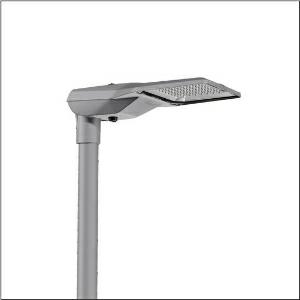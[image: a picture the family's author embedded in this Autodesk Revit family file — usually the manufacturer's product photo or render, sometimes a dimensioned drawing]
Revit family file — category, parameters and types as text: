
# Revit family: streetlight_sl_21_iq_midi___pc-l_5xe3f31y08mb_244c
name_source: partatom
category: Lighting Fixtures
units: mm (PartAtom-declared; Revit-internal decimal feet)

## family parameters
Cut with Voids When Loaded = No
Host = Face
Light Source = No
Part Type = Normal
Room Calculation Point = No
Round Connector Dimension = Use Diameter
Shared = No

## types (1)
- --- (1 x LED, 17070 lm, 129.3 W, 3000K)
    Apparent Load = 129 VA
    CIE Flux Codes = 38 78 98 100 100
    Color Rendering = 70
    Color Temperature = 3000K
    Default Elevation = 1800 mm
    Description = Streetlight SL 21 iQ midi, mast luminaire, primary light control with lens, of PMMA, primary optical cover: cover, of toughened safety glass, transparent, light distribution: PC-L, light emission: direct distribution, primary light characteristic: asymmetric, left, installation type: post-top, side-entry, LED, High Power LED, rated luminous flux: 17.070lm, luminous efficacy: 132lm/W, light colour: 730, colour temperature: 3000K, control gear: iQ-Street Remote, D4i with power reduction, control: pre-setting: logarithmic dimming characteristic, Street-Remote, Auto-Match, Temp-Guard, Lumen-Switch, Night-Set, Smart-Wire, Light-Fading, Desk-Remote (wireless, voltage-free reading and setting of iQ features in the workshop via application-optimized NFC function/RFID function), optimised constant luminous flux control (CLO 2.0), mains connection: 230..240V, AC, 50/60Hz, start of lifetime: 129W, end of service life: 142W, reduction: 56W, luminaire housing, of diecast aluminium, powder-coated, Siteco® metallic grey (DB 702S), corrosivity category C5 mid according to DIN EN ISO 12944, please order mast flange separately, inclination adjustable: 0°, 5°, 10°, 15°, sealing non-destructively replaceable, multi-level sealing system, length: 644mm, width: 335mm, height: 110mm, mast flange for spigot size: 42mm (side-entry): 5XC10008XM4, 60/48mm (side-entry/post-top): 5XC10108XM2, 76/60mm (side-entry/post-top): 5XC10108XM1, mounting height: 4..8m, Smart Interface below and above, protection rating (complete): IP66, insulation class (complete): insulation class II (safety insulation), certification: CE, ENEC, ENEC+, VDE, impact resistance: IK10, permissible operating ambient temperature for outdoor applications: -40..+50°C, standard-compliant lighting for roads and squares, packaging unit: 1 piece

Light Distribution: PC-L
    Height = 111 mm
    Lamp = 1 x LED
    Lamp Light Flux = 17070 lm
    Lamp Power = 129.3 W
    Lamp count = 1
    Length = 644 mm
    Luminous efficacy = 132 lm/W
    Manufacturer = Siteco
    ModVariant = No
    Model = 5XE3F31Y08MB
    Number of Poles = 1
    OnlyDefault = Yes
    Power Factor = 1
    Product Name = Streetlight SL 21 iQ midi | PC-L
    Product group = mast luminaire | pylon top
    ProductGroupID = 6100
    Protection Class = Protection class II
    Protection Degree = IP 66
    RLX_Detail_Level = 1
    RLX_Emergency_Light_Flux = 0 lm
    RLX_Emergency_Type = 0
    RLX_Emergency_Type_DB = No
    RlxData = <blob elided: 29881 chars, md5=6737fbea>
    Socket = socket
    Standby Power = 0 W
    System Light Flux = 17070 lm
    System Power = 129 W
    Type Comments = factory setting: luminous flux: 100 % | dim-lin: 254 | 672 mA
    Type Image = l_1004304.jpg
    URL = http://relux.com
    VarID = @adj_085953
    Voltage = 0 V
    Weight = 0.00 kg
    Width = 336 mm

## geometry (parser evidence)
native form markers: Blend x4, Sweep x9
no freeform markers — native parametric forms only
